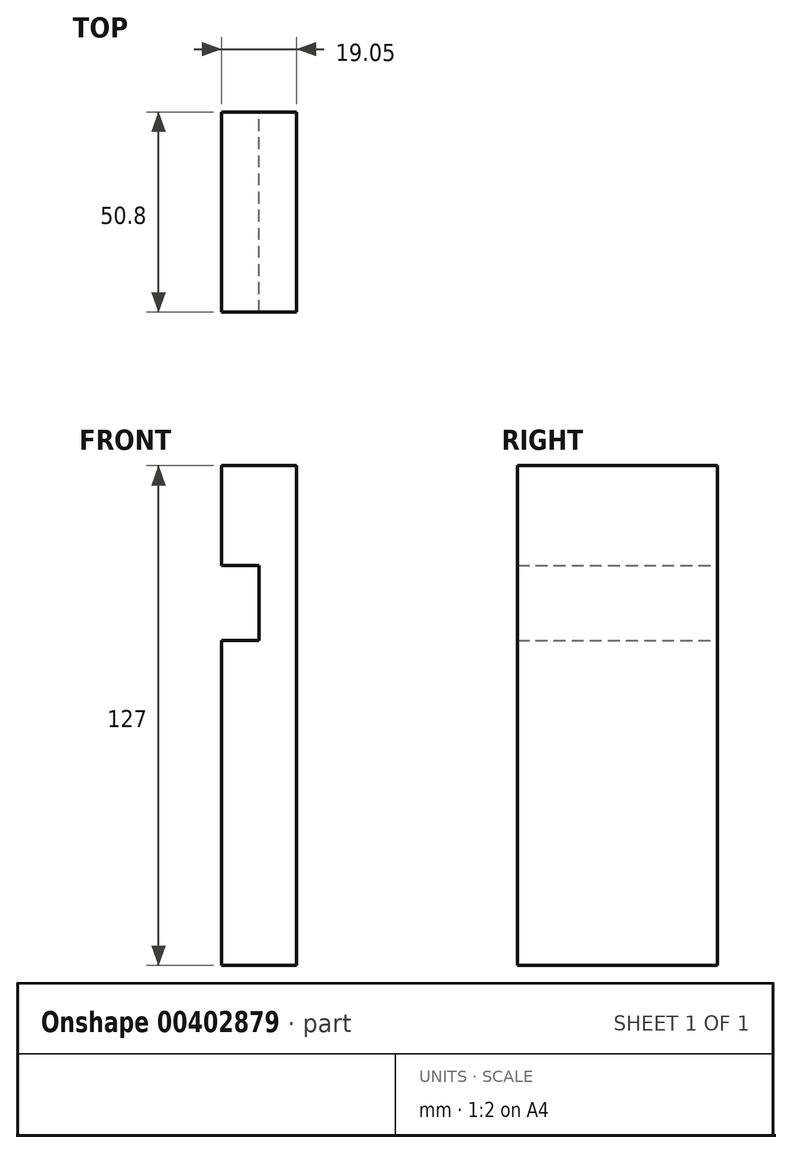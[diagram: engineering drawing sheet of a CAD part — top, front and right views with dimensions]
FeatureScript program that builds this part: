
annotation { "Feature Type Name" : "Feature", "Feature Type Description" : "" }
export const myFeature = defineFeature(function(context is Context, id is Id, definition is map)
    precondition{}
    {
        {
            var Q0;
            Q0=qCreatedBy(makeId("Front.planeOp"),FACE);
            var sketch = newSketch(context, id + "F0", { "sketchPlane" : qUnion([Q0])});
            skLineSegment(sketch, "E0", {"start": v(0, 0) * mm, "end": v(0, 63.5) * mm});
            skLineSegment(sketch, "E1", {"start": v(0, 0) * mm, "end": v(0, -63.5) * mm});
            skLineSegment(sketch, "E2", {"start": v(0, 63.5) * mm, "end": v(-19.05, 63.5) * mm});
            skLineSegment(sketch, "E3", {"start": v(0, -63.5) * mm, "end": v(-19.05, -63.5) * mm});
            skLineSegment(sketch, "E4", {"start": v(-19.05, 63.5) * mm, "end": v(-19.05, 38.1) * mm});
            skLineSegment(sketch, "E5", {"start": v(-19.05, 38.1) * mm, "end": v(-9.52, 38.1) * mm});
            skLineSegment(sketch, "E6", {"start": v(-9.52, 38.1) * mm, "end": v(-9.52, 19.05) * mm});
            skLineSegment(sketch, "E7", {"start": v(-9.52, 19.05) * mm, "end": v(-19.05, 19.05) * mm});
            skLineSegment(sketch, "E8", {"start": v(-19.05, 19.05) * mm, "end": v(-19.05, -63.5) * mm});
            skSolve(sketch);
        }
        {
            var Q0;
            Q0 = qSketchRegion(id + "F0", true);
            extrude(context, id + "F1", {"entities" : qUnion([Q0]), "depth" : 50.8 * mm});
        }
    });
